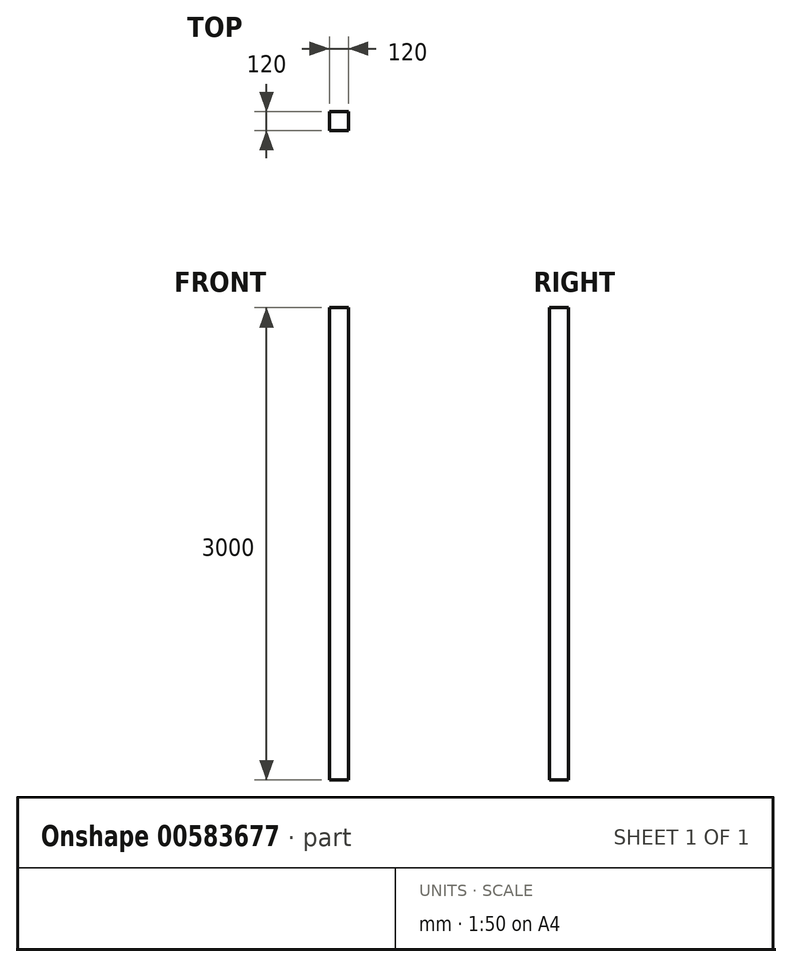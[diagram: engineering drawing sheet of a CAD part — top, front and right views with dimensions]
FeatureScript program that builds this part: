
annotation { "Feature Type Name" : "Feature", "Feature Type Description" : "" }
export const myFeature = defineFeature(function(context is Context, id is Id, definition is map)
    precondition{}
    {
        {
            var Q0;
            Q0=qCreatedBy(makeId("Top.planeOp"),FACE);
            var sketch = newSketch(context, id + "F0", { "sketchPlane" : qUnion([Q0])});
            skLineSegment(sketch, "E0.bottom", {"start": v(60, 60) * mm, "end": v(-60, 60) * mm});
            skLineSegment(sketch, "E0.top", {"start": v(60, -60) * mm, "end": v(-60, -60) * mm});
            skLineSegment(sketch, "E0.left", {"start": v(60, 60) * mm, "end": v(60, -60) * mm});
            skLineSegment(sketch, "E0.right", {"start": v(-60, 60) * mm, "end": v(-60, -60) * mm});
            skPoint(sketch, "E0.middle", {"position": v(0, 0) * mm});
            skSolve(sketch);
        }
        {
            var Q0;
            Q0 = qSketchRegion(id + "F0", true);
            extrude(context, id + "F1", {"entities" : qUnion([Q0]), "depth" : 3000 * mm, "offsetDistance" : 25 * mm});
        }
    });
